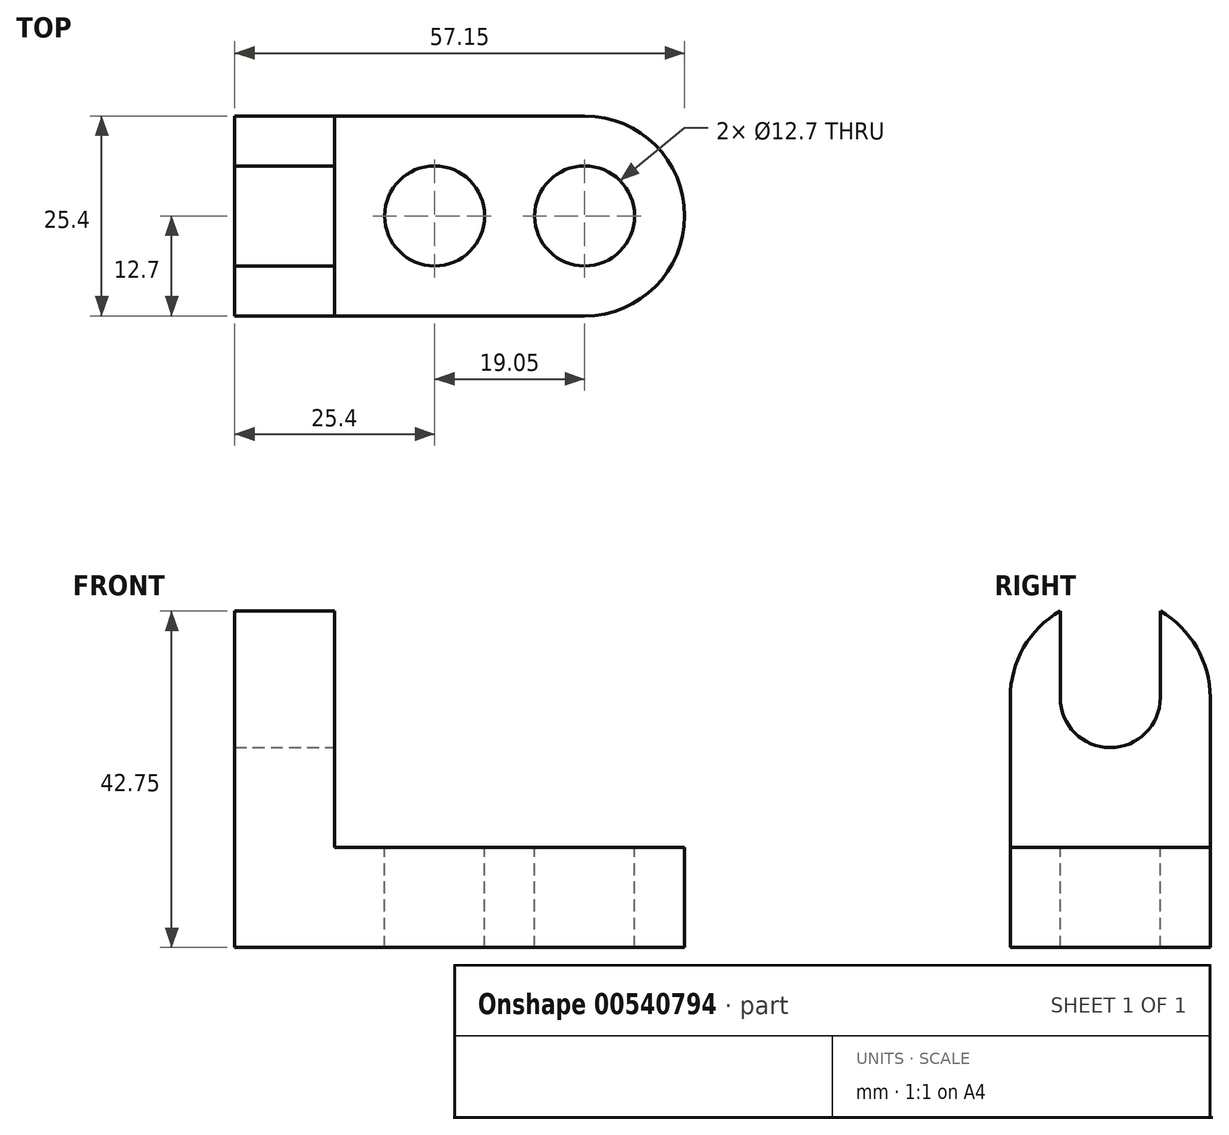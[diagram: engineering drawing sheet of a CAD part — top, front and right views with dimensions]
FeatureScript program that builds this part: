
annotation { "Feature Type Name" : "Feature", "Feature Type Description" : "" }
export const myFeature = defineFeature(function(context is Context, id is Id, definition is map)
    precondition{}
    {
        {
            var Q0;
            Q0=qCreatedBy(makeId("Front.planeOp"),FACE);
            var sketch = newSketch(context, id + "F0", { "sketchPlane" : qUnion([Q0])});
            skLineSegment(sketch, "E0", {"start": v(0, 0) * mm, "end": v(57.15, 0) * mm});
            skLineSegment(sketch, "E1", {"start": v(57.15, 0) * mm, "end": v(57.15, 12.7) * mm});
            skLineSegment(sketch, "E2", {"start": v(57.15, 12.7) * mm, "end": v(12.7, 12.7) * mm});
            skLineSegment(sketch, "E3", {"start": v(12.7, 12.7) * mm, "end": v(12.7, 44.45) * mm});
            skLineSegment(sketch, "E4", {"start": v(12.7, 44.45) * mm, "end": v(0, 44.45) * mm});
            skLineSegment(sketch, "E5", {"start": v(0, 44.45) * mm, "end": v(0, 0) * mm});
            skSolve(sketch);
        }
        {
            var Q0;
            Q0=makeQuery(id+"F0.imprint","IMPRINT",FACE,{"disambiguationData":[TD([[makeQuery(id+"F0.imprint","IMPRINT",EDGE,{"derivedFrom":sQuery(id+"F0.wireOp",EDGE,"E0")}),1.0]])]});
            extrude(context, id + "F1", {"entities" : qUnion([Q0]), "depth" : 25.4 * mm, "offsetDistance" : 25.4 * mm});
        }
        {
            var Q0;
            Q0=makeQuery(id+"F1.opExtrude","SWEPT_FACE",FACE,{"disambiguationData":[OSD([sQuery(id+"F0.wireOp",EDGE,"E2")])]});
            var sketch = newSketch(context, id + "F2", { "sketchPlane" : qUnion([Q0])});
            skCircle(sketch, "E6", {"center": v(44.45, -12.7) * mm, "radius": 6.35 * mm});
            skCircle(sketch, "E7", {"center": v(25.4, -12.7) * mm, "radius": 6.35 * mm});
            skArc(sketch, "E8", {"start": v(44.45, -25.4) * mm, "mid": v(57.15, -12.7) * mm, "end": v(44.45, 0) * mm});
            skSolve(sketch);
        }
        {
            var Q0;
            Q0=makeQuery(id+"F2.imprint","IMPRINT",FACE,{"disambiguationData":[TD([[makeQuery(id+"F2.imprint","IMPRINT",EDGE,{"derivedFrom":sQuery(id+"F2.wireOp",EDGE,"E7")}),1.0]])]});
            var Q1;
            Q1=makeQuery(id+"F2.imprint","IMPRINT",FACE,{"disambiguationData":[TD([[makeQuery(id+"F2.imprint","IMPRINT",EDGE,{"derivedFrom":sQuery(id+"F2.wireOp",EDGE,"E6")}),1.0]])]});
            var Q2;
            {var subQ0=sQuery(id+"F2.wireOp",EDGE,"E8");var subQ1=sQuery(id+"F0.wireOp",EDGE,"E2");var subQ2=makeQuery(id+"F1.opExtrude","CAP_EDGE",EDGE,{"disambiguationData":[OSD([subQ1])],"isStart":false});var subQ3=makeQuery(id+"F2.imprint","INTERSECT",VERTEX,{"derivedFrom":[subQ2,subQ0]});Q2=makeQuery(id+"F2.imprint","IMPRINT",FACE,{"disambiguationData":[TD([[makeQuery(id+"F2.imprint","IMPRINT",EDGE,{"disambiguationData":[TD([[subQ3,-1.0]])],"derivedFrom":subQ0}),-1.0]])]});}
            var Q3;
            {var subQ0=sQuery(id+"F2.wireOp",EDGE,"E8");var subQ1=sQuery(id+"F0.wireOp",EDGE,"E2");var subQ2=makeQuery(id+"F1.opExtrude","CAP_EDGE",EDGE,{"disambiguationData":[OSD([subQ1])],"isStart":true});var subQ3=makeQuery(id+"F2.imprint","INTERSECT",VERTEX,{"derivedFrom":[subQ2,subQ0]});Q3=makeQuery(id+"F2.imprint","IMPRINT",FACE,{"disambiguationData":[TD([[makeQuery(id+"F2.imprint","IMPRINT",EDGE,{"disambiguationData":[TD([[subQ3,1.0]])],"derivedFrom":subQ0}),-1.0]])]});}
            extrude(context, id + "F3", {"entities" : qUnion([Q0, Q1, Q2, Q3]), "operationType" : NewBodyOperationType.REMOVE, "oppositeDirection" : true, "depth" : 12.7 * mm, "offsetDistance" : 25.4 * mm});
        }
        {
            var Q0;
            Q0=makeQuery(id+"F1.opExtrude","SWEPT_FACE",FACE,{"disambiguationData":[OSD([sQuery(id+"F0.wireOp",EDGE,"E3")])]});
            var sketch = newSketch(context, id + "F4", { "sketchPlane" : qUnion([Q0])});
            skCircle(sketch, "E9", {"center": v(-12.7, 31.75) * mm, "radius": 6.35 * mm});
            skLineSegment(sketch, "E10", {"start": v(-6.35, 31.75) * mm, "end": v(-6.35, 44.45) * mm});
            skLineSegment(sketch, "E11", {"start": v(-19.05, 31.75) * mm, "end": v(-19.05, 44.45) * mm});
            skArc(sketch, "E12", {"start": v(0, 31.75) * mm, "mid": v(-12.7, 44.45) * mm, "end": v(-25.4, 31.75) * mm});
            skSolve(sketch);
        }
        {
            var Q0;
            {var subQ0=sQuery(id+"F4.wireOp",EDGE,"E9");var subQ1=makeQuery(id+"F4.imprint","INTERSECT",VERTEX,{"derivedFrom":[subQ0,sQuery(id+"F4.wireOp",EDGE,"E10")]});Q0=makeQuery(id+"F4.imprint","IMPRINT",FACE,{"disambiguationData":[TD([[makeQuery(id+"F4.imprint","IMPRINT",EDGE,{"disambiguationData":[TD([[subQ1,-1.0]])],"derivedFrom":subQ0}),1.0]])]});}
            var Q1;
            {var subQ1=sQuery(id+"F4.wireOp",EDGE,"E9");var subQ5=sQuery(id+"F4.wireOp",EDGE,"E10");var subQ8=makeQuery(id+"F4.imprint","INTERSECT",VERTEX,{"derivedFrom":[subQ1,subQ5]});Q1=makeQuery(id+"F4.imprint","IMPRINT",FACE,{"disambiguationData":[TD([[makeQuery(id+"F4.imprint","IMPRINT",EDGE,{"disambiguationData":[TD([[subQ8,-1.0]])],"derivedFrom":subQ1}),-1.0]])]});}
            var Q2;
            {var subQ1=sQuery(id+"F0.wireOp",EDGE,"E3");var subQ4=sQuery(id+"F4.wireOp",EDGE,"E12");var subQ6=makeQuery(id+"F1.opExtrude","CAP_EDGE",EDGE,{"disambiguationData":[OSD([subQ1])],"isStart":true});var subQ7=makeQuery(id+"F4.imprint","INTERSECT",VERTEX,{"derivedFrom":[subQ6,subQ4]});Q2=makeQuery(id+"F4.imprint","IMPRINT",FACE,{"disambiguationData":[TD([[makeQuery(id+"F4.imprint","IMPRINT",EDGE,{"disambiguationData":[TD([[subQ7,-1.0]])],"derivedFrom":subQ4}),-1.0]])]});}
            var Q3;
            {var subQ1=sQuery(id+"F0.wireOp",EDGE,"E3");var subQ4=sQuery(id+"F4.wireOp",EDGE,"E12");var subQ6=makeQuery(id+"F1.opExtrude","CAP_EDGE",EDGE,{"disambiguationData":[OSD([subQ1])],"isStart":false});var subQ7=makeQuery(id+"F4.imprint","INTERSECT",VERTEX,{"derivedFrom":[subQ6,subQ4]});Q3=makeQuery(id+"F4.imprint","IMPRINT",FACE,{"disambiguationData":[TD([[makeQuery(id+"F4.imprint","IMPRINT",EDGE,{"disambiguationData":[TD([[subQ7,1.0]])],"derivedFrom":subQ4}),-1.0]])]});}
            var Q4;
            {var subQ0=sQuery(id+"F4.wireOp",EDGE,"E11");var subQ3=sQuery(id+"F4.wireOp",EDGE,"E12");var subQ4=makeQuery(id+"F4.imprint","INTERSECT",VERTEX,{"derivedFrom":[subQ0,subQ3]});Q4=makeQuery(id+"F4.imprint","IMPRINT",FACE,{"disambiguationData":[TD([[makeQuery(id+"F4.imprint","IMPRINT",EDGE,{"disambiguationData":[TD([[subQ4,-1.0]])],"derivedFrom":subQ0}),-1.0]])]});}
            var Q5;
            {var subQ0=sQuery(id+"F4.wireOp",EDGE,"E10");var subQ3=sQuery(id+"F4.wireOp",EDGE,"E12");var subQ4=makeQuery(id+"F4.imprint","INTERSECT",VERTEX,{"derivedFrom":[subQ0,subQ3]});Q5=makeQuery(id+"F4.imprint","IMPRINT",FACE,{"disambiguationData":[TD([[makeQuery(id+"F4.imprint","IMPRINT",EDGE,{"disambiguationData":[TD([[subQ4,-1.0]])],"derivedFrom":subQ0}),1.0]])]});}
            extrude(context, id + "F5", {"entities" : qUnion([Q0, Q1, Q2, Q3, Q4, Q5]), "operationType" : NewBodyOperationType.REMOVE, "oppositeDirection" : true, "depth" : 12.7 * mm, "offsetDistance" : 25.4 * mm});
        }
    });
